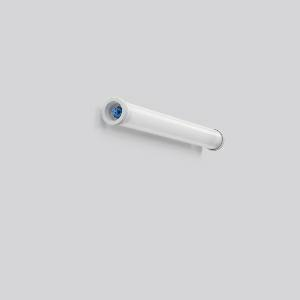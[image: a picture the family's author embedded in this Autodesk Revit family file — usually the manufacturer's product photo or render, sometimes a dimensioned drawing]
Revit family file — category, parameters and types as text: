
# Revit family: planox_tube_601070_002_1_730hf_92a6
name_source: partatom
category: Lighting Fixtures
units: mm (PartAtom-declared; Revit-internal decimal feet)

## family parameters
Cut with Voids When Loaded = No
Host = Face
Light Source = No
Part Type = Normal
Room Calculation Point = No
Round Connector Dimension = Use Diameter
Shared = No

## types (1)
- PLANOX TUBE (1 x LED Modul 840, 3500 lm, 4000)
    Apparent Load = 31 VA
    CIE Flux Codes = 41 70 89 89 100
    Color Rendering = 80
    Color Temperature = 4000
    Default Elevation = 1800 mm
    Description = Series: PLANOX TUBE
Robust protective tube luminaire for tough requirements. Rack made of sheet steel, white powder coated. End caps made of plastic (polyamide) grey. Diffuser made of plastic (polycarbonate), opal, shockproof. Symmetrical light distribution. Homogeneous light distribution. With accessories for wall, ceiling or pendant mounting. Suitable for through-wiring. With integrated HF movement sensor. Movement sensor functional parameters: Hold time: can be set with Casambi app. Range: up to 6 m, adjustable in 4 steps. Brightness sensor: adjustable in 5 steps. Factory setting: hold time adjustable via Casambi app, brightness threshold deactivated, detection range 100%. Mounting set must be ordered separately. Luminaire with limited surface temperature in accordance with EN 60598-2-24 for use in environments in which a deposit of conductive dust on the luminaire can be expected. Qualified for use in the food and drink industry. Suitable for lighting in public car parks and public off-street parking spaces according to DIN 67528. Environmentally friendly and resource-saving due to replaceable components. 
Colour: white
Diameter: 78 mm
Length: 792 mm
Lamp: LED
Socket: without socket
Colour temperature: 4000K
Colour rendering index (CRI): 83
System power: 31 W
Rated luminous flux: 3500 lm
Luminous efficiency: 113 lm/W
Control gear: Dimmable Bluetooth converter
Protection class: I
Type of protection: IP 67
    Height = 0 mm  [stored 0 ft]
    Lamp = 1 x LED Modul 840
    Lamp Light Flux = 3500 lm
    Lamp count = 1
    Length = 792 mm
    Lifetime = 50000 h
    Luminous efficacy = 113 lm/W
    Manufacturer = RZB
    ModVariant = No
    Model = 601070.002.1.730HF
    Mounting Place = Ceiling, Wall
    Mounting Type = Surface mounted
    Number of Poles = 1
    OnlyDefault = Yes
    Power Factor = 1
    Product Name = PLANOX TUBE
    Product group = Surface mounted luminaires for moist/humid enviroments
    ProductGroupID = 308
    Protection Class = Protection class I
    Protection Degree = Degree of protection
    RLX_Detail_Level = 1
    RLX_Emergency_Light_Flux = 0 lm
    RLX_Emergency_Type = 0
    RLX_Emergency_Type_DB = No
    RlxData = <blob elided: 31777 chars, md5=42e69a13>
    Socket = socket
    Standby Power = 0 W
    System Light Flux = 3500 lm
    System Power = 31 W
    Type Comments = Product without accessories
    Type Image = 601070.002.jpg
    URL = http://relux.com
    VarID = ---
    Voltage = 230 V
    Voltage Range = 220-240 V
    Weight = 0.00 kg
    Width = 0 mm  [stored 0 ft]

note: [stored X ft] marks values corroborated as IEEE doubles in the binary element streams (Revit-internal decimal feet)

## geometry (parser evidence)
native form markers: Blend x4, Sweep x13
no freeform markers — native parametric forms only
